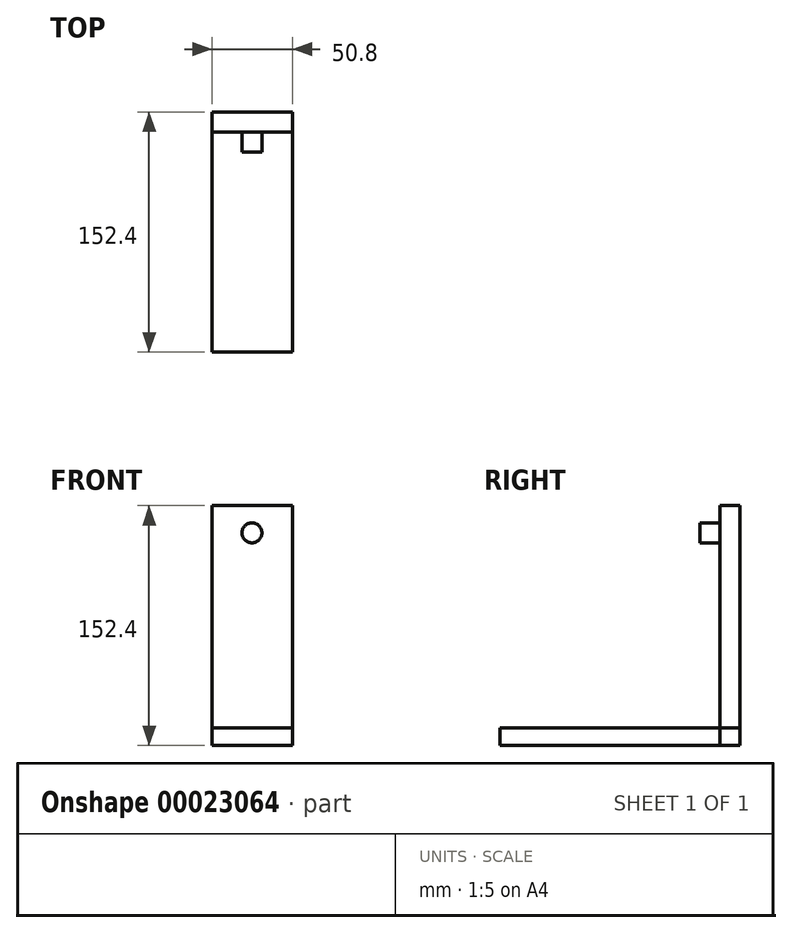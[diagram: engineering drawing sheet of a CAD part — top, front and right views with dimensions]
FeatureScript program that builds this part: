
annotation { "Feature Type Name" : "Feature", "Feature Type Description" : "" }
export const myFeature = defineFeature(function(context is Context, id is Id, definition is map)
    precondition{}
    {
        {
            var Q0;
            Q0=qCreatedBy(makeId("Front.planeOp"),FACE);
            var sketch = newSketch(context, id + "F0", { "sketchPlane" : qUnion([Q0])});
            skLineSegment(sketch, "E0.bottom", {"start": v(0, 0) * mm, "end": v(50.8, 0) * mm});
            skLineSegment(sketch, "E0.top", {"start": v(0, 152.4) * mm, "end": v(50.8, 152.4) * mm});
            skLineSegment(sketch, "E0.left", {"start": v(0, 0) * mm, "end": v(0, 152.4) * mm});
            skLineSegment(sketch, "E0.right", {"start": v(50.8, 0) * mm, "end": v(50.8, 152.4) * mm});
            skLineSegment(sketch, "E1", {"start": v(50.8, 11.15) * mm, "end": v(0, 11.15) * mm});
            skSolve(sketch);
        }
        {
            var Q0;
            Q0=makeQuery(id+"F0.imprint","IMPRINT",FACE,{"disambiguationData":[TD([[makeQuery(id+"F0.imprint","IMPRINT",EDGE,{"derivedFrom":sQuery(id+"F0.wireOp",EDGE,"E0.bottom")}),1.0]])]});
            extrude(context, id + "F1", {"entities" : qUnion([Q0]), "depth" : 12.7 * mm});
        }
        {
            var Q0;
            Q0=makeQuery(id+"F1.opExtrude","CAP_FACE",FACE,{"disambiguationData":[OSD([sQuery(id+"F0.wireOp",EDGE,"E0.bottom"),sQuery(id+"F0.wireOp",EDGE,"E0.top"),sQuery(id+"F0.wireOp",EDGE,"E0.left"),sQuery(id+"F0.wireOp",EDGE,"E0.right")])],"isStart":false});
            var sketch = newSketch(context, id + "F2", { "sketchPlane" : qUnion([Q0])});
            skCircle(sketch, "E2", {"center": v(25.2, 135.05) * mm, "radius": 6.35 * mm});
            skSolve(sketch);
        }
        {
            var Q0;
            Q0=makeQuery(id+"F2.imprint","IMPRINT",FACE,{"disambiguationData":[TD([[makeQuery(id+"F2.imprint","IMPRINT",EDGE,{"derivedFrom":sQuery(id+"F2.wireOp",EDGE,"E2")}),1.0]])]});
            extrude(context, id + "F3", {"entities" : qUnion([Q0]), "operationType" : NewBodyOperationType.ADD, "depth" : 12.7 * mm});
        }
        {
            var Q0;
            Q0 = qSketchRegion(id + "F0", true);
            extrude(context, id + "F4", {"entities" : qUnion([Q0]), "depth" : 12.7 * mm});
        }
        {
            var Q0;
            Q0=makeQuery(id+"F2.imprint","IMPRINT",FACE,{"disambiguationData":[TD([[makeQuery(id+"F2.imprint","IMPRINT",EDGE,{"derivedFrom":makeQuery(id+"F1.opExtrude","CAP_EDGE",EDGE,{"disambiguationData":[OSD([sQuery(id+"F0.wireOp",EDGE,"E0.bottom")])],"isStart":false})}),1.0]])]});
            extrude(context, id + "F5", {"entities" : qUnion([Q0]), "depth" : 139.7 * mm});
        }
    });
